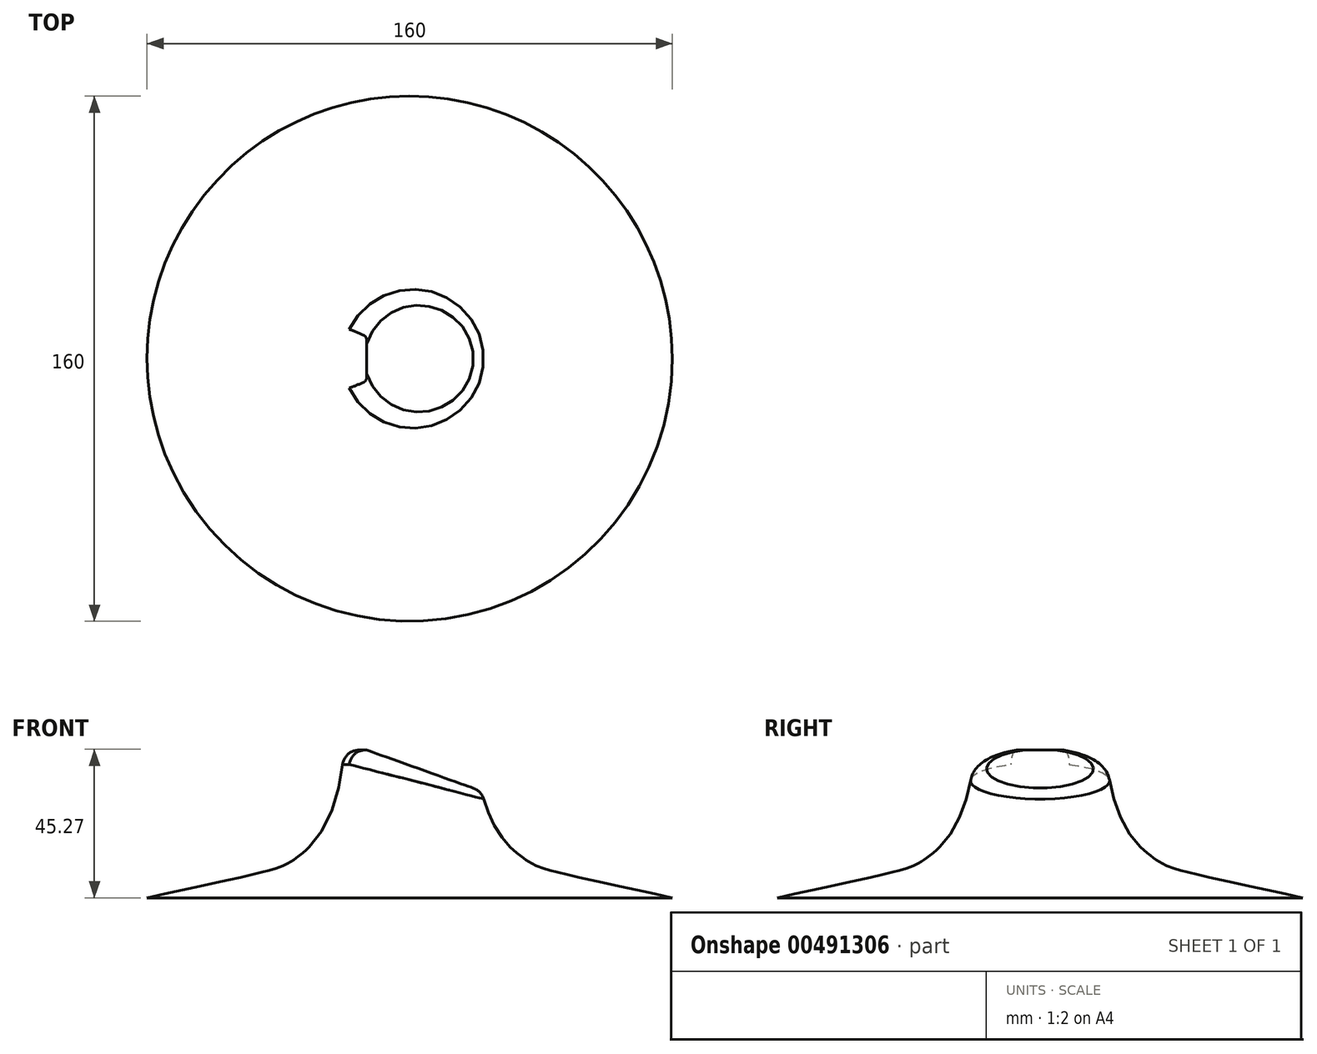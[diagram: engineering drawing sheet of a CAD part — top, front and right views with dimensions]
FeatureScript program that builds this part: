
annotation { "Feature Type Name" : "Feature", "Feature Type Description" : "" }
export const myFeature = defineFeature(function(context is Context, id is Id, definition is map)
    precondition{}
    {
        {
            var Q0;
            Q0=qCreatedBy(makeId("Front.planeOp"),FACE);
            var sketch = newSketch(context, id + "F0", { "sketchPlane" : qUnion([Q0])});
            skFitSpline(sketch, "E0", {"points": [v(-80, 0) * mm, v(-34.56, 12.13) * mm, v(-20, 45) * mm], "startDerivative": vector(211.88, 47.62) * mm, "endDerivative": vector(10.3, 142.53) * mm});
            skLineSegment(sketch, "E1", {"start": v(-20, 45) * mm, "end": v(0, 45) * mm});
            skLineSegment(sketch, "E2", {"start": v(0, 45) * mm, "end": v(0, 0) * mm});
            skLineSegment(sketch, "E3", {"start": v(0, 0) * mm, "end": v(-80, 0) * mm});
            skSolve(sketch);
        }
        {
            var Q0;
            Q0 = qSketchRegion(id + "F0", true);
            var Q1;
            Q1=sQuery(id+"F0.wireOp",EDGE,"E2");
            revolve(context, id + "F1", {"entities" : qUnion([Q0]), "axis" : qUnion([Q1]), "revolveType" : RevolveType.FULL});
        }
        {
            var Q0;
            Q0=qCreatedBy(makeId("Front.planeOp"),FACE);
            var sketch = newSketch(context, id + "F2", { "sketchPlane" : qUnion([Q0])});
            skLineSegment(sketch, "E4", {"start": v(-54.31, 59.74) * mm, "end": v(72.16, 14.54) * mm});
            skLineSegment(sketch, "E5", {"start": v(72.16, 14.54) * mm, "end": v(60.13, 61.48) * mm});
            skLineSegment(sketch, "E6", {"start": v(60.13, 61.48) * mm, "end": v(-54.31, 59.74) * mm});
            skSolve(sketch);
        }
        {
            var Q0;
            Q0 = qSketchRegion(id + "F2", true);
            extrude(context, id + "F3", {"entities" : qUnion([Q0]), "operationType" : NewBodyOperationType.REMOVE, "endBound" : BoundingType.SYMMETRIC, "oppositeDirection" : true, "depth" : 100 * mm});
        }
        {
            var Q0;
            Q0=makeQuery(id+"F3.boolean.opBoolean","INTERSECT",EDGE,{"derivedFrom":[makeQuery(id+"F1.opRevolve","SWEPT_FACE",FACE,{"disambiguationData":[OSD([sQuery(id+"F0.wireOp",EDGE,"E0")])]}),makeQuery(id+"F3.opExtrude","SWEPT_FACE",FACE,{"disambiguationData":[OSD([sQuery(id+"F2.wireOp",EDGE,"E4")])]})]});
            var Q1;
            Q1=makeQuery(id+"F1.opRevolve","SWEPT_EDGE",EDGE,{"disambiguationData":[OSD([sQuery(id+"F0.wireOp",EDGE,"E0"),sQuery(id+"F0.wireOp",EDGE,"E1")])]});
            fillet(context, id + "F4", {"entities" : qUnion([Q0, Q1]), "radius" : 5 * mm, "tangentPropagation" : true, "allowEdgeOverflow" : false});
        }
    });
